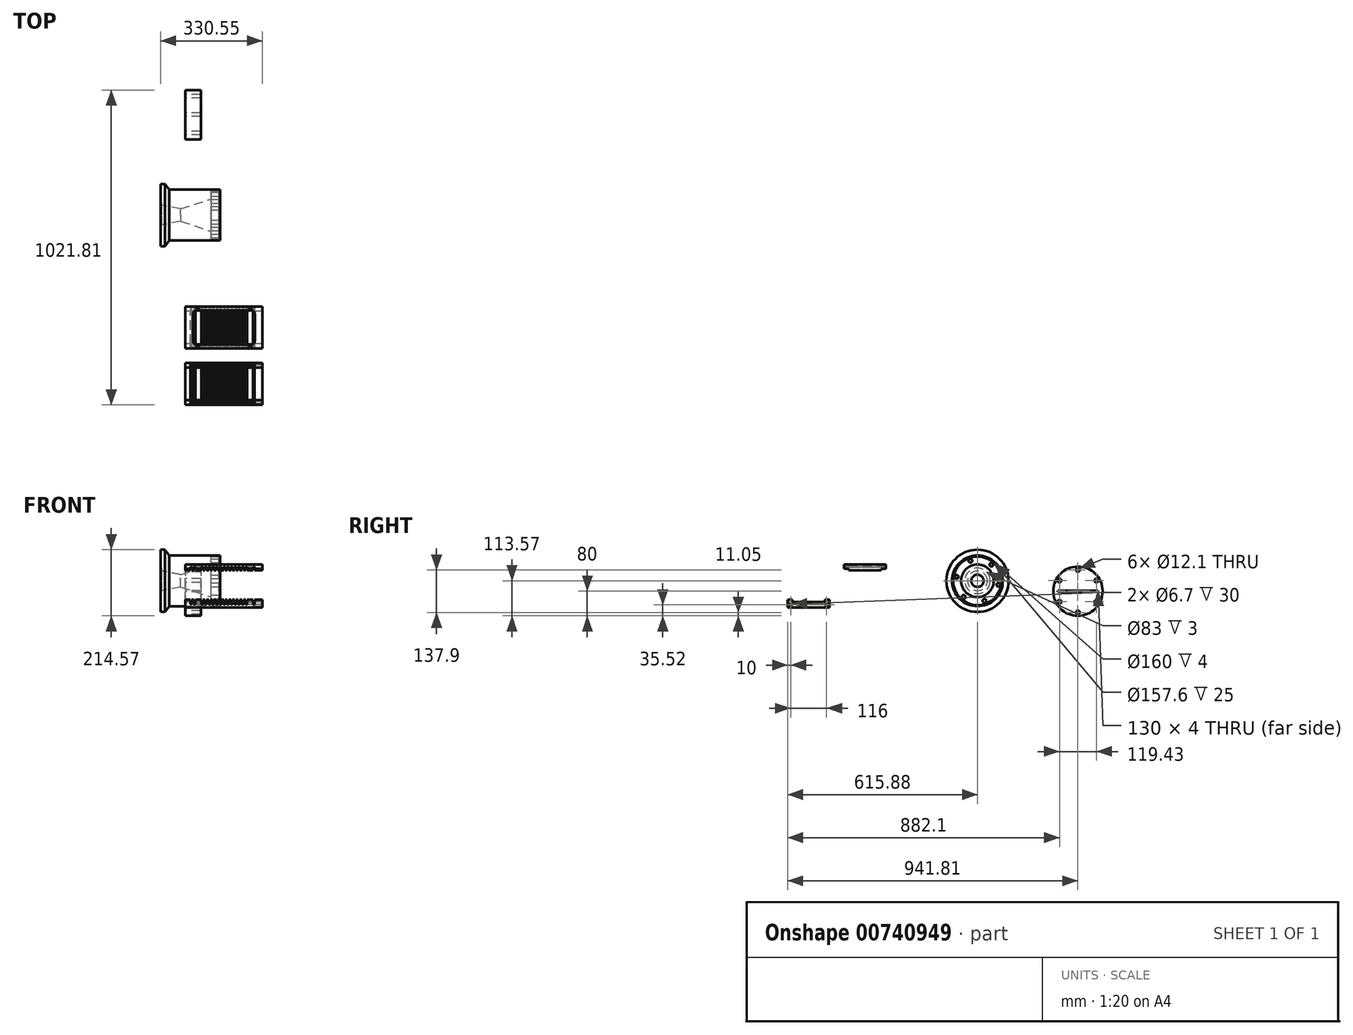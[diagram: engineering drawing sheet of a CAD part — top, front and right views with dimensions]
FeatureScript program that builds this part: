
annotation { "Feature Type Name" : "Feature", "Feature Type Description" : "" }
export const myFeature = defineFeature(function(context is Context, id is Id, definition is map)
    precondition{}
    {
        {
            var Q0;
            Q0=qCreatedBy(makeId("Front.planeOp"),FACE);
            var sketch = newSketch(context, id + "F0", { "sketchPlane" : qUnion([Q0])});
            skLineSegment(sketch, "E0", {"start": v(-80.55, 124) * mm, "end": v(-80.55, 183.5) * mm});
            skLineSegment(sketch, "E1", {"start": v(-80.55, 183.5) * mm, "end": v(-66.55, 183.5) * mm});
            skLineSegment(sketch, "E2", {"start": v(-66.55, 183.5) * mm, "end": v(-52.88, 165) * mm});
            skLineSegment(sketch, "E3", {"start": v(-52.88, 165) * mm, "end": v(-37.88, 165) * mm});
            skLineSegment(sketch, "E4", {"start": v(112.12, 162.5) * mm, "end": v(112.12, 165) * mm});
            skLineSegment(sketch, "E5", {"start": v(112.12, 165) * mm, "end": v(-37.88, 165) * mm});
            skPoint(sketch, "E6.endSnap0", {"position": v(-80.55, 82.5) * mm});
            skLineSegment(sketch, "E7", {"start": v(-261.09, 82.5) * mm, "end": v(-80.55, 82.5) * mm});
            skLineSegment(sketch, "E8", {"start": v(-80.55, 124) * mm, "end": v(-77.55, 124) * mm});
            skLineSegment(sketch, "E9", {"start": v(-77.55, 124) * mm, "end": v(-77.55, 114.5) * mm});
            skLineSegment(sketch, "E10", {"start": v(-77.55, 114.5) * mm, "end": v(-15.38, 102.5) * mm});
            skLineSegment(sketch, "E11", {"start": v(-15.38, 102.5) * mm, "end": v(108.12, 143.67) * mm});
            skPoint(sketch, "E12.orphan", {"position": v(112.12, 82.5) * mm});
            skLineSegment(sketch, "E13.trimOffspring", {"start": v(112.12, 82.5) * mm, "end": v(310.1, 82.5) * mm});
            skLineSegment(sketch, "E14", {"start": v(112.12, 162.5) * mm, "end": v(108.12, 162.5) * mm});
            skLineSegment(sketch, "E15", {"start": v(108.12, 162.5) * mm, "end": v(108.12, 143.67) * mm});
            skPoint(sketch, "E16.orphan", {"position": v(112.12, 145) * mm});
            skSolve(sketch);
        }
        {
            var Q0;
            Q0=makeQuery(id+"F0.imprint","IMPRINT",FACE,{"disambiguationData":[TD([[makeQuery(id+"F0.imprint","IMPRINT",EDGE,{"derivedFrom":sQuery(id+"F0.wireOp",EDGE,"E1")}),-1.0]])]});
            var Q1;
            Q1=sQuery(id+"F0.wireOp",EDGE,"E13.trimOffspring");
            revolve(context, id + "F1", {"entities" : qUnion([Q0]), "axis" : qUnion([Q1]), "revolveType" : RevolveType.ONE_DIRECTION, "angle" : 360 * degree});
        }
        {
            var Q0;
            Q0=makeQuery(id+"F1.opRevolve","SWEPT_FACE",FACE,{"disambiguationData":[OSD([sQuery(id+"F0.wireOp",EDGE,"E15")])]});
            var sketch = newSketch(context, id + "F2", { "sketchPlane" : qUnion([Q0])});
            skSolve(sketch);
        }
        {
            var Q0;
            {var subQ0=sQuery(id+"F0.wireOp",EDGE,"E15");Q0=makeQuery(id+"F2.imprint","IMPRINT",FACE,{"disambiguationData":[TD([[makeQuery(id+"F2.imprint","IMPRINT",EDGE,{"derivedFrom":makeQuery(id+"F1.opRevolve","SWEPT_EDGE",EDGE,{"disambiguationData":[OSD([sQuery(id+"F0.wireOp",EDGE,"E11"),subQ0])]})}),1.0]])]});}
            var sketch = newSketch(context, id + "F3", { "sketchPlane" : qUnion([Q0])});
            skCircle(sketch, "E17", {"center": v(-22.8, 147.57) * mm, "radius": 6 * mm});
            skPoint(sketch, "E18.third.point", {"position": v(-56.7, 43.27) * mm});
            skCircle(sketch, "E19.1.0", {"center": v(-67.75, 95.29) * mm, "radius": 6 * mm});
            skCircle(sketch, "E19.2.0", {"center": v(-44.95, 30.22) * mm, "radius": 6 * mm});
            skCircle(sketch, "E19.3.0", {"center": v(22.8, 17.43) * mm, "radius": 6 * mm});
            skCircle(sketch, "E19.4.0", {"center": v(67.75, 69.71) * mm, "radius": 6 * mm});
            skCircle(sketch, "E19.5.0", {"center": v(44.95, 134.78) * mm, "radius": 6 * mm});
            skPoint(sketch, "E19.center", {"position": v(0, 82.5) * mm});
            skCircle(sketch, "E20", {"center": v(0, 82.5) * mm, "radius": 78.8 * mm});
            skSolve(sketch);
        }
        {
            var Q0;
            Q0=qSketchRegion(id+"F3",true);
            extrude(context, id + "F4", {"entities" : qUnion([Q0]), "operationType" : NewBodyOperationType.REMOVE, "oppositeDirection" : true, "depth" : 25 * mm});
        }
        {
            var Q0;
            Q0=qCreatedBy(makeId("Right.planeOp"),FACE);
            var sketch = newSketch(context, id + "F5", { "sketchPlane" : qUnion([Q0])});
            skCircle(sketch, "E21", {"center": v(325.93, 48.93) * mm, "radius": 80 * mm});
            skLineSegment(sketch, "E22.bottom", {"start": v(260.93, 50.93) * mm, "end": v(390.93, 50.93) * mm});
            skLineSegment(sketch, "E22.top", {"start": v(260.93, 46.93) * mm, "end": v(390.93, 46.93) * mm});
            skLineSegment(sketch, "E22.left", {"start": v(260.93, 50.93) * mm, "end": v(260.93, 46.93) * mm});
            skLineSegment(sketch, "E22.right", {"start": v(390.93, 50.93) * mm, "end": v(390.93, 46.93) * mm});
            skLineSegment(sketch, "E23", {"start": v(325.93, 148.9) * mm, "end": v(325.93, -70.52) * mm, "construction": true});
            skCircle(sketch, "E24", {"center": v(325.93, 117.88) * mm, "radius": 6.05 * mm});
            skCircle(sketch, "E25.1.0", {"center": v(266.22, 83.4) * mm, "radius": 6.05 * mm});
            skCircle(sketch, "E25.2.0", {"center": v(266.22, 14.46) * mm, "radius": 6.05 * mm});
            skCircle(sketch, "E25.3.0", {"center": v(325.93, -20.02) * mm, "radius": 6.05 * mm});
            skCircle(sketch, "E25.4.0", {"center": v(385.65, 14.46) * mm, "radius": 6.05 * mm});
            skCircle(sketch, "E25.5.0", {"center": v(385.65, 83.4) * mm, "radius": 6.05 * mm});
            skSolve(sketch);
        }
        {
            var Q0;
            Q0 = qSketchRegion(id + "F5", true);
            extrude(context, id + "F6", {"entities" : qUnion([Q0]), "depth" : 50 * mm, "offsetDistance" : 25 * mm});
        }
        {
            var Q0;
            Q0=qCreatedBy(makeId("Right.planeOp"),FACE);
            var sketch = newSketch(context, id + "F7", { "sketchPlane" : qUnion([Q0])});
            skLineSegment(sketch, "E26.top", {"start": v(-494.88, 13.45) * mm, "end": v(-600.88, 13.45) * mm});
            skLineSegment(sketch, "E26.left", {"start": v(-494.88, 16.45) * mm, "end": v(-494.88, 13.45) * mm});
            skLineSegment(sketch, "E26.right", {"start": v(-600.88, 16.45) * mm, "end": v(-600.88, 13.45) * mm});
            skPoint(sketch, "E26.middle", {"position": v(-547.88, 14.95) * mm});
            skLineSegment(sketch, "E27", {"start": v(-494.88, 21.45) * mm, "end": v(-484.88, 21.45) * mm});
            skLineSegment(sketch, "E28", {"start": v(-479.88, 16.45) * mm, "end": v(-479.88, -3.55) * mm});
            skLineSegment(sketch, "E29", {"start": v(-547.88, 69.6) * mm, "end": v(-547.88, -62.33) * mm});
            skLineSegment(sketch, "E30", {"start": v(-479.88, -3.55) * mm, "end": v(-547.88, -3.55) * mm});
            skLineSegment(sketch, "E31", {"start": v(-494.88, 16.45) * mm, "end": v(-494.88, 21.45) * mm});
            skLineSegment(sketch, "E32.MirrorCS", {"start": v(-600.88, 16.45) * mm, "end": v(-600.88, 21.45) * mm});
            skLineSegment(sketch, "E33.MirrorCS", {"start": v(-600.88, 21.45) * mm, "end": v(-610.88, 21.45) * mm});
            skLineSegment(sketch, "E34.MirrorCS", {"start": v(-615.88, 16.45) * mm, "end": v(-615.88, -3.55) * mm});
            skLineSegment(sketch, "E35.MirrorCS", {"start": v(-615.88, -3.55) * mm, "end": v(-547.88, -3.55) * mm});
            skLineSegment(sketch, "E36.bottom", {"start": v(-311.68, 116.16) * mm, "end": v(-417.68, 116.16) * mm});
            skLineSegment(sketch, "E36.left", {"start": v(-311.68, 116.16) * mm, "end": v(-311.68, 113.16) * mm});
            skLineSegment(sketch, "E37", {"start": v(-311.68, 121.16) * mm, "end": v(-301.68, 121.16) * mm});
            skLineSegment(sketch, "E38", {"start": v(-311.68, 116.16) * mm, "end": v(-311.68, 121.16) * mm});
            skLineSegment(sketch, "E39.MirrorCS", {"start": v(-417.68, 116.16) * mm, "end": v(-417.68, 121.16) * mm});
            skLineSegment(sketch, "E40.MirrorCS", {"start": v(-417.68, 121.16) * mm, "end": v(-427.68, 121.16) * mm});
            skLineSegment(sketch, "E41", {"start": v(-432.68, 136.16) * mm, "end": v(-296.68, 136.16) * mm});
            skLineSegment(sketch, "E42", {"start": v(-296.68, 136.16) * mm, "end": v(-296.68, 121.16) * mm});
            skLineSegment(sketch, "E43", {"start": v(-364.68, 136.16) * mm, "end": v(-364.68, 116.16) * mm});
            skPoint(sketch, "E43.startSnap0", {"position": v(-364.68, 116.16) * mm});
            skLineSegment(sketch, "E44.MirrorCS", {"start": v(-432.68, 136.16) * mm, "end": v(-432.68, 121.16) * mm});
            skLineSegment(sketch, "E45", {"start": v(-301.68, 121.16) * mm, "end": v(-296.68, 121.16) * mm});
            skPoint(sketch, "E46.orphan", {"position": v(-296.68, 116.16) * mm});
            skPoint(sketch, "E47.end.orphan", {"position": v(-301.68, 116.16) * mm});
            skLineSegment(sketch, "E48", {"start": v(-427.68, 121.16) * mm, "end": v(-432.68, 121.16) * mm});
            skPoint(sketch, "E49.MirrorCS.end.orphan", {"position": v(-427.68, 116.16) * mm});
            skPoint(sketch, "E49.MirrorCS.start.orphan", {"position": v(-427.68, 121.16) * mm});
            skPoint(sketch, "E50.MirrorCS.end.orphan", {"position": v(-432.68, 116.16) * mm});
            skLineSegment(sketch, "E51", {"start": v(-484.88, 21.45) * mm, "end": v(-479.88, 21.45) * mm});
            skLineSegment(sketch, "E52", {"start": v(-479.88, 21.45) * mm, "end": v(-479.88, 16.45) * mm});
            skPoint(sketch, "E53.start.orphan", {"position": v(-484.88, 16.45) * mm});
            skLineSegment(sketch, "E54", {"start": v(-615.88, 16.45) * mm, "end": v(-615.88, 21.45) * mm});
            skLineSegment(sketch, "E55", {"start": v(-615.88, 21.45) * mm, "end": v(-610.88, 21.45) * mm});
            skPoint(sketch, "E56.MirrorCS.end.orphan", {"position": v(-610.88, 16.45) * mm});
            skSolve(sketch);
        }
        {
            var Q0;
            Q0 = qSketchRegion(id + "F7", true);
            extrude(context, id + "F8", {"entities" : qUnion([Q0]), "depth" : 250 * mm, "offsetDistance" : 25 * mm});
        }
        {
            var Q0;
            Q0=makeQuery(id+"F8.opExtrude","SWEPT_FACE",FACE,{"disambiguationData":[OSD([sQuery(id+"F7.wireOp",EDGE,"E41")])]});
            var sketch = newSketch(context, id + "F9", { "sketchPlane" : qUnion([Q0])});
            skPoint(sketch, "E57.startSnap0", {"position": v(0, -364.68) * mm});
            skLineSegment(sketch, "E58.bottom", {"start": v(215, -419.68) * mm, "end": v(35, -419.68) * mm});
            skLineSegment(sketch, "E58.top", {"start": v(215, -309.68) * mm, "end": v(35, -309.68) * mm});
            skLineSegment(sketch, "E58.left", {"start": v(225, -409.68) * mm, "end": v(225, -319.68) * mm});
            skLineSegment(sketch, "E58.right", {"start": v(25, -409.68) * mm, "end": v(25, -319.68) * mm});
            skPoint(sketch, "E58.middle", {"position": v(125, -364.68) * mm});
            skPoint(sketch, "E59.start.orphan", {"position": v(125, -296.68) * mm});
            skPoint(sketch, "E57.start.orphan", {"position": v(-23.66, -364.68) * mm});
            skPoint(sketch, "E60.visualSharp", {"position": v(25, -309.68) * mm});
            skArc(sketch, "E60.filletArc", {"start": v(35, -309.68) * mm, "mid": v(27.93, -312.6) * mm, "end": v(25, -319.68) * mm});
            skPoint(sketch, "E61.visualSharp", {"position": v(25, -419.68) * mm});
            skArc(sketch, "E61.filletArc", {"start": v(25, -409.68) * mm, "mid": v(27.93, -416.75) * mm, "end": v(35, -419.68) * mm});
            skPoint(sketch, "E62.visualSharp", {"position": v(225, -419.68) * mm});
            skArc(sketch, "E62.filletArc", {"start": v(215, -419.68) * mm, "mid": v(222.07, -416.75) * mm, "end": v(225, -409.68) * mm});
            skPoint(sketch, "E63.visualSharp", {"position": v(225, -309.68) * mm});
            skArc(sketch, "E63.filletArc", {"start": v(225, -319.68) * mm, "mid": v(222.07, -312.6) * mm, "end": v(215, -309.68) * mm});
            skSolve(sketch);
        }
        {
            var Q0;
            Q0 = qSketchRegion(id + "F9", true);
            extrude(context, id + "F10", {"entities" : qUnion([Q0]), "operationType" : NewBodyOperationType.REMOVE, "oppositeDirection" : true, "depth" : 10 * mm, "offsetDistance" : 25 * mm});
        }
        {
            var Q0;
            Q0=makeQuery(id+"F8.opExtrude","SWEPT_FACE",FACE,{"disambiguationData":[OSD([sQuery(id+"F7.wireOp",EDGE,"E30"),sQuery(id+"F7.wireOp",EDGE,"E35.MirrorCS")])]});
            var sketch = newSketch(context, id + "F11", { "sketchPlane" : qUnion([Q0])});
            skLineSegment(sketch, "E64.bottom", {"start": v(35, 602.88) * mm, "end": v(215, 602.88) * mm});
            skLineSegment(sketch, "E64.top", {"start": v(35, 492.88) * mm, "end": v(215, 492.88) * mm});
            skLineSegment(sketch, "E64.left", {"start": v(25, 592.88) * mm, "end": v(25, 502.88) * mm});
            skLineSegment(sketch, "E64.right", {"start": v(225, 592.88) * mm, "end": v(225, 502.88) * mm});
            skPoint(sketch, "E64.middle", {"position": v(125, 547.88) * mm});
            skPoint(sketch, "E65.visualSharp", {"position": v(25, 602.88) * mm});
            skArc(sketch, "E65.filletArc", {"start": v(35, 602.88) * mm, "mid": v(27.93, 599.95) * mm, "end": v(25, 592.88) * mm});
            skPoint(sketch, "E66.visualSharp", {"position": v(25, 492.88) * mm});
            skArc(sketch, "E66.filletArc", {"start": v(25, 502.88) * mm, "mid": v(27.93, 495.8) * mm, "end": v(35, 492.88) * mm});
            skPoint(sketch, "E67.visualSharp", {"position": v(225, 492.88) * mm});
            skArc(sketch, "E67.filletArc", {"start": v(215, 492.88) * mm, "mid": v(222.07, 495.8) * mm, "end": v(225, 502.88) * mm});
            skPoint(sketch, "E68.visualSharp", {"position": v(225, 602.88) * mm});
            skArc(sketch, "E68.filletArc", {"start": v(225, 592.88) * mm, "mid": v(222.07, 599.95) * mm, "end": v(215, 602.88) * mm});
            skPoint(sketch, "E69.orphan", {"position": v(125, 615.88) * mm});
            skPoint(sketch, "E70.start.orphan", {"position": v(0, 547.88) * mm});
            skSolve(sketch);
        }
        {
            var Q0;
            Q0 = qSketchRegion(id + "F11", true);
            extrude(context, id + "F12", {"entities" : qUnion([Q0]), "operationType" : NewBodyOperationType.REMOVE, "oppositeDirection" : true, "depth" : 10 * mm, "offsetDistance" : 25 * mm});
        }
        {
            var Q0;
            Q0=makeQuery(id+"F8.opExtrude","CAP_FACE",FACE,{"disambiguationData":[OSD([sQuery(id+"F7.wireOp",EDGE,"E26.bottom"),sQuery(id+"F7.wireOp",EDGE,"E27"),sQuery(id+"F7.wireOp",EDGE,"C7VJGF0Z-FXYF-PAxQ-nA2d-aZA8GV4GVZuc"),sQuery(id+"F7.wireOp",EDGE,"E53"),sQuery(id+"F7.wireOp",EDGE,"E28"),sQuery(id+"F7.wireOp",EDGE,"E30"),sQuery(id+"F7.wireOp",EDGE,"E31"),sQuery(id+"F7.wireOp",EDGE,"E32.MirrorCS"),sQuery(id+"F7.wireOp",EDGE,"E33.MirrorCS"),sQuery(id+"F7.wireOp",EDGE,"E56.MirrorCS"),sQuery(id+"F7.wireOp",EDGE,"2c69a955-ea22-4fbe-a683-bcde0f60a3190.MirrorCS"),sQuery(id+"F7.wireOp",EDGE,"E34.MirrorCS"),sQuery(id+"F7.wireOp",EDGE,"E35.MirrorCS")])],"isStart":false});
            var sketch = newSketch(context, id + "F13", { "sketchPlane" : qUnion([Q0])});
            skCircle(sketch, "E71", {"center": v(-605.88, 4.45) * mm, "radius": 3.35 * mm});
            skCircle(sketch, "E72", {"center": v(-489.88, 4.45) * mm, "radius": 3.35 * mm});
            skSolve(sketch);
        }
        {
            var Q0;
            Q0 = qSketchRegion(id + "F13", true);
            extrude(context, id + "F14", {"entities" : qUnion([Q0]), "operationType" : NewBodyOperationType.REMOVE, "oppositeDirection" : true, "depth" : 30 * mm, "offsetDistance" : 25 * mm});
        }
        {
            var Q0;
            Q0=makeQuery(id+"F8.opExtrude","SWEPT_FACE",FACE,{"disambiguationData":[OSD([sQuery(id+"F7.wireOp",EDGE,"E33.MirrorCS"),sQuery(id+"F7.wireOp",EDGE,"E55")])]});
            var sketch = newSketch(context, id + "F15", { "sketchPlane" : qUnion([Q0])});
            skCircle(sketch, "E73", {"center": v(210, -487.38) * mm, "radius": 3.35 * mm});
            skCircle(sketch, "E74", {"center": v(40, -487.38) * mm, "radius": 3.35 * mm});
            skCircle(sketch, "E75", {"center": v(210, -608.38) * mm, "radius": 3.35 * mm});
            skCircle(sketch, "E76", {"center": v(40, -608.38) * mm, "radius": 3.35 * mm});
            skSolve(sketch);
        }
        {
            var Q0;
            Q0=makeQuery(id+"F15.imprint","IMPRINT",FACE,{"disambiguationData":[TD([[makeQuery(id+"F15.imprint","IMPRINT",EDGE,{"derivedFrom":sQuery(id+"F15.wireOp",EDGE,"E73")}),1.0]])]});
            var Q1;
            Q1=makeQuery(id+"F15.imprint","IMPRINT",FACE,{"disambiguationData":[TD([[makeQuery(id+"F15.imprint","IMPRINT",EDGE,{"derivedFrom":sQuery(id+"F15.wireOp",EDGE,"E74")}),1.0]])]});
            var Q2;
            Q2=makeQuery(id+"F15.imprint","IMPRINT",FACE,{"disambiguationData":[TD([[makeQuery(id+"F15.imprint","IMPRINT",EDGE,{"derivedFrom":sQuery(id+"F15.wireOp",EDGE,"E76")}),1.0]])]});
            var Q3;
            Q3=makeQuery(id+"F15.imprint","IMPRINT",FACE,{"disambiguationData":[TD([[makeQuery(id+"F15.imprint","IMPRINT",EDGE,{"derivedFrom":sQuery(id+"F15.wireOp",EDGE,"E75")}),1.0]])]});
            extrude(context, id + "F16", {"entities" : qUnion([Q0, Q1, Q2, Q3]), "operationType" : NewBodyOperationType.REMOVE, "oppositeDirection" : true, "depth" : 10 * mm, "offsetDistance" : 25 * mm});
        }
        {
            var Q0;
            Q0=makeQuery(id+"F8.opExtrude","SWEPT_FACE",FACE,{"disambiguationData":[OSD([sQuery(id+"F7.wireOp",EDGE,"E41")])]});
            var sketch = newSketch(context, id + "F17", { "sketchPlane" : qUnion([Q0])});
            skLineSegment(sketch, "E77.bottom", {"start": v(40, -304.18) * mm, "end": v(210, -304.18) * mm});
            skLineSegment(sketch, "E77.top", {"start": v(40, -425.18) * mm, "end": v(210, -425.18) * mm});
            skLineSegment(sketch, "E77.left", {"start": v(40, -304.18) * mm, "end": v(40, -425.18) * mm});
            skLineSegment(sketch, "E77.right", {"start": v(210, -304.18) * mm, "end": v(210, -425.18) * mm});
            skPoint(sketch, "E77.middle", {"position": v(125, -364.68) * mm});
            skPoint(sketch, "E77.middle.positionSnap0", {"position": v(125, -296.68) * mm});
            skPoint(sketch, "E77.middle.positionSnap1", {"position": v(0, -364.68) * mm});
            skPoint(sketch, "E77.centerSnap0", {"position": v(125, -296.68) * mm});
            skPoint(sketch, "E77.centerSnap1", {"position": v(0, -364.68) * mm});
            skCircle(sketch, "E78", {"center": v(210, -304.18) * mm, "radius": 4 * mm});
            skCircle(sketch, "E79", {"center": v(40, -304.18) * mm, "radius": 4 * mm});
            skCircle(sketch, "E80", {"center": v(40, -425.18) * mm, "radius": 4 * mm});
            skCircle(sketch, "E81", {"center": v(210, -425.18) * mm, "radius": 4 * mm});
            skSolve(sketch);
        }
        {
            var Q0;
            {var subQ0=sQuery(id+"F17.wireOp",EDGE,"E77.left");var subQ1=sQuery(id+"F17.wireOp",EDGE,"E77.top");var subQ2=makeQuery(id+"F17.imprint","INTERSECT",VERTEX,{"derivedFrom":[subQ1,subQ0]});Q0=makeQuery(id+"F17.imprint","IMPRINT",FACE,{"disambiguationData":[TD([[makeQuery(id+"F17.imprint","IMPRINT",EDGE,{"disambiguationData":[TD([[subQ2,-1.0]])],"derivedFrom":subQ1}),-1.0]])]});}
            var Q1;
            {var subQ0=sQuery(id+"F17.wireOp",EDGE,"E77.left");var subQ1=sQuery(id+"F17.wireOp",EDGE,"E77.top");var subQ2=makeQuery(id+"F17.imprint","INTERSECT",VERTEX,{"derivedFrom":[subQ1,subQ0]});Q1=makeQuery(id+"F17.imprint","IMPRINT",FACE,{"disambiguationData":[TD([[makeQuery(id+"F17.imprint","IMPRINT",EDGE,{"disambiguationData":[TD([[subQ2,-1.0]])],"derivedFrom":subQ1}),1.0]])]});}
            var Q2;
            {var subQ0=sQuery(id+"F17.wireOp",EDGE,"E77.right");var subQ1=sQuery(id+"F17.wireOp",EDGE,"E77.top");var subQ2=makeQuery(id+"F17.imprint","INTERSECT",VERTEX,{"derivedFrom":[subQ1,subQ0]});Q2=makeQuery(id+"F17.imprint","IMPRINT",FACE,{"disambiguationData":[TD([[makeQuery(id+"F17.imprint","IMPRINT",EDGE,{"disambiguationData":[TD([[subQ2,1.0]])],"derivedFrom":subQ1}),-1.0]])]});}
            var Q3;
            {var subQ0=sQuery(id+"F17.wireOp",EDGE,"E77.right");var subQ1=sQuery(id+"F17.wireOp",EDGE,"E77.top");var subQ2=makeQuery(id+"F17.imprint","INTERSECT",VERTEX,{"derivedFrom":[subQ1,subQ0]});Q3=makeQuery(id+"F17.imprint","IMPRINT",FACE,{"disambiguationData":[TD([[makeQuery(id+"F17.imprint","IMPRINT",EDGE,{"disambiguationData":[TD([[subQ2,1.0]])],"derivedFrom":subQ1}),1.0]])]});}
            var Q4;
            {var subQ0=sQuery(id+"F17.wireOp",EDGE,"E77.right");var subQ1=sQuery(id+"F17.wireOp",EDGE,"E77.bottom");var subQ2=makeQuery(id+"F17.imprint","INTERSECT",VERTEX,{"derivedFrom":[subQ1,subQ0]});Q4=makeQuery(id+"F17.imprint","IMPRINT",FACE,{"disambiguationData":[TD([[makeQuery(id+"F17.imprint","IMPRINT",EDGE,{"disambiguationData":[TD([[subQ2,1.0]])],"derivedFrom":subQ1}),1.0]])]});}
            var Q5;
            {var subQ0=sQuery(id+"F17.wireOp",EDGE,"E77.right");var subQ1=sQuery(id+"F17.wireOp",EDGE,"E77.bottom");var subQ2=makeQuery(id+"F17.imprint","INTERSECT",VERTEX,{"derivedFrom":[subQ1,subQ0]});Q5=makeQuery(id+"F17.imprint","IMPRINT",FACE,{"disambiguationData":[TD([[makeQuery(id+"F17.imprint","IMPRINT",EDGE,{"disambiguationData":[TD([[subQ2,1.0]])],"derivedFrom":subQ1}),-1.0]])]});}
            var Q6;
            {var subQ0=sQuery(id+"F17.wireOp",EDGE,"E77.left");var subQ1=sQuery(id+"F17.wireOp",EDGE,"E77.bottom");var subQ2=makeQuery(id+"F17.imprint","INTERSECT",VERTEX,{"derivedFrom":[subQ1,subQ0]});Q6=makeQuery(id+"F17.imprint","IMPRINT",FACE,{"disambiguationData":[TD([[makeQuery(id+"F17.imprint","IMPRINT",EDGE,{"disambiguationData":[TD([[subQ2,-1.0]])],"derivedFrom":subQ1}),1.0]])]});}
            var Q7;
            {var subQ0=sQuery(id+"F17.wireOp",EDGE,"E77.left");var subQ1=sQuery(id+"F17.wireOp",EDGE,"E77.bottom");var subQ2=makeQuery(id+"F17.imprint","INTERSECT",VERTEX,{"derivedFrom":[subQ1,subQ0]});Q7=makeQuery(id+"F17.imprint","IMPRINT",FACE,{"disambiguationData":[TD([[makeQuery(id+"F17.imprint","IMPRINT",EDGE,{"disambiguationData":[TD([[subQ2,-1.0]])],"derivedFrom":subQ1}),-1.0]])]});}
            extrude(context, id + "F18", {"entities" : qUnion([Q0, Q1, Q2, Q3, Q4, Q5, Q6, Q7]), "operationType" : NewBodyOperationType.REMOVE, "oppositeDirection" : true, "depth" : 25 * mm, "offsetDistance" : 25 * mm});
        }
        {
            var Q0;
            Q0=makeQuery(id+"F9.imprint","IMPRINT",FACE,{"disambiguationData":[TD([[makeQuery(id+"F9.imprint","IMPRINT",EDGE,{"derivedFrom":sQuery(id+"F9.wireOp",EDGE,"E58.bottom")}),-1.0]])]});
            extrude(context, id + "F19", {"entities" : qUnion([Q0]), "operationType" : NewBodyOperationType.REMOVE, "oppositeDirection" : true, "depth" : 8 * mm, "offsetDistance" : 25 * mm});
        }
        {
            var Q0;
            Q0=makeQuery(id+"F8.opExtrude","SWEPT_FACE",FACE,{"disambiguationData":[OSD([sQuery(id+"F7.wireOp",EDGE,"E34.MirrorCS"),sQuery(id+"F7.wireOp",EDGE,"E54")])]});
            var sketch = newSketch(context, id + "F20", { "sketchPlane" : qUnion([Q0])});
            skLineSegment(sketch, "E82", {"start": v(250, -3.55) * mm, "end": v(250, 163.65) * mm});
            skLineSegment(sketch, "E83", {"start": v(250, 163.65) * mm, "end": v(235, 163.65) * mm});
            skLineSegment(sketch, "E84", {"start": v(235, 163.65) * mm, "end": v(235, -3.55) * mm});
            skLineSegment(sketch, "E85", {"start": v(235, -3.55) * mm, "end": v(250, -3.55) * mm});
            skLineSegment(sketch, "E86", {"start": v(224.5, -3.55) * mm, "end": v(224.5, 163.65) * mm});
            skLineSegment(sketch, "E87", {"start": v(224.5, 163.65) * mm, "end": v(219.5, 163.65) * mm});
            skLineSegment(sketch, "E88", {"start": v(219.5, 163.65) * mm, "end": v(219.5, -3.55) * mm});
            skLineSegment(sketch, "E89", {"start": v(219.5, -3.55) * mm, "end": v(224.5, -3.55) * mm});
            skLineSegment(sketch, "E90.1.0.0", {"start": v(212.5, -3.55) * mm, "end": v(212.5, 163.65) * mm});
            skLineSegment(sketch, "E90.1.0.1", {"start": v(207.5, 163.65) * mm, "end": v(207.5, -3.55) * mm});
            skLineSegment(sketch, "E90.1.0.2", {"start": v(212.5, 163.65) * mm, "end": v(207.5, 163.65) * mm});
            skLineSegment(sketch, "E90.1.0.3", {"start": v(207.5, -3.55) * mm, "end": v(212.5, -3.55) * mm});
            skLineSegment(sketch, "E90.2.0.0", {"start": v(200.5, -3.55) * mm, "end": v(200.5, 163.65) * mm});
            skLineSegment(sketch, "E90.2.0.1", {"start": v(195.5, 163.65) * mm, "end": v(195.5, -3.55) * mm});
            skLineSegment(sketch, "E90.2.0.2", {"start": v(200.5, 163.65) * mm, "end": v(195.5, 163.65) * mm});
            skLineSegment(sketch, "E90.2.0.3", {"start": v(195.5, -3.55) * mm, "end": v(200.5, -3.55) * mm});
            skLineSegment(sketch, "E90.3.0.0", {"start": v(188.5, -3.55) * mm, "end": v(188.5, 163.65) * mm});
            skLineSegment(sketch, "E90.3.0.1", {"start": v(183.5, 163.65) * mm, "end": v(183.5, -3.55) * mm});
            skLineSegment(sketch, "E90.3.0.2", {"start": v(188.5, 163.65) * mm, "end": v(183.5, 163.65) * mm});
            skLineSegment(sketch, "E90.3.0.3", {"start": v(183.5, -3.55) * mm, "end": v(188.5, -3.55) * mm});
            skLineSegment(sketch, "E90.4.0.0", {"start": v(176.5, -3.55) * mm, "end": v(176.5, 163.65) * mm});
            skLineSegment(sketch, "E90.4.0.1", {"start": v(171.5, 163.65) * mm, "end": v(171.5, -3.55) * mm});
            skLineSegment(sketch, "E90.4.0.2", {"start": v(176.5, 163.65) * mm, "end": v(171.5, 163.65) * mm});
            skLineSegment(sketch, "E90.4.0.3", {"start": v(171.5, -3.55) * mm, "end": v(176.5, -3.55) * mm});
            skLineSegment(sketch, "E90.5.0.0", {"start": v(164.5, -3.55) * mm, "end": v(164.5, 163.65) * mm});
            skLineSegment(sketch, "E90.5.0.1", {"start": v(159.5, 163.65) * mm, "end": v(159.5, -3.55) * mm});
            skLineSegment(sketch, "E90.5.0.2", {"start": v(164.5, 163.65) * mm, "end": v(159.5, 163.65) * mm});
            skLineSegment(sketch, "E90.5.0.3", {"start": v(159.5, -3.55) * mm, "end": v(164.5, -3.55) * mm});
            skLineSegment(sketch, "E90.6.0.0", {"start": v(152.5, -3.55) * mm, "end": v(152.5, 163.65) * mm});
            skLineSegment(sketch, "E90.6.0.1", {"start": v(147.5, 163.65) * mm, "end": v(147.5, -3.55) * mm});
            skLineSegment(sketch, "E90.6.0.2", {"start": v(152.5, 163.65) * mm, "end": v(147.5, 163.65) * mm});
            skLineSegment(sketch, "E90.6.0.3", {"start": v(147.5, -3.55) * mm, "end": v(152.5, -3.55) * mm});
            skLineSegment(sketch, "E90.7.0.0", {"start": v(140.5, -3.55) * mm, "end": v(140.5, 163.65) * mm});
            skLineSegment(sketch, "E90.7.0.1", {"start": v(135.5, 163.65) * mm, "end": v(135.5, -3.55) * mm});
            skLineSegment(sketch, "E90.7.0.2", {"start": v(140.5, 163.65) * mm, "end": v(135.5, 163.65) * mm});
            skLineSegment(sketch, "E90.7.0.3", {"start": v(135.5, -3.55) * mm, "end": v(140.5, -3.55) * mm});
            skLineSegment(sketch, "E90.8.0.0", {"start": v(128.5, -3.55) * mm, "end": v(128.5, 163.65) * mm});
            skLineSegment(sketch, "E90.8.0.1", {"start": v(123.5, 163.65) * mm, "end": v(123.5, -3.55) * mm});
            skLineSegment(sketch, "E90.8.0.2", {"start": v(128.5, 163.65) * mm, "end": v(123.5, 163.65) * mm});
            skLineSegment(sketch, "E90.8.0.3", {"start": v(123.5, -3.55) * mm, "end": v(128.5, -3.55) * mm});
            skLineSegment(sketch, "E90.9.0.0", {"start": v(116.5, -3.55) * mm, "end": v(116.5, 163.65) * mm});
            skLineSegment(sketch, "E90.9.0.1", {"start": v(111.5, 163.65) * mm, "end": v(111.5, -3.55) * mm});
            skLineSegment(sketch, "E90.9.0.2", {"start": v(116.5, 163.65) * mm, "end": v(111.5, 163.65) * mm});
            skLineSegment(sketch, "E90.9.0.3", {"start": v(111.5, -3.55) * mm, "end": v(116.5, -3.55) * mm});
            skLineSegment(sketch, "E90.10.0.0", {"start": v(104.5, -3.55) * mm, "end": v(104.5, 163.65) * mm});
            skLineSegment(sketch, "E90.10.0.1", {"start": v(99.5, 163.65) * mm, "end": v(99.5, -3.55) * mm});
            skLineSegment(sketch, "E90.10.0.2", {"start": v(104.5, 163.65) * mm, "end": v(99.5, 163.65) * mm});
            skLineSegment(sketch, "E90.10.0.3", {"start": v(99.5, -3.55) * mm, "end": v(104.5, -3.55) * mm});
            skLineSegment(sketch, "E90.11.0.0", {"start": v(92.5, -3.55) * mm, "end": v(92.5, 163.65) * mm});
            skLineSegment(sketch, "E90.11.0.1", {"start": v(87.5, 163.65) * mm, "end": v(87.5, -3.55) * mm});
            skLineSegment(sketch, "E90.11.0.2", {"start": v(92.5, 163.65) * mm, "end": v(87.5, 163.65) * mm});
            skLineSegment(sketch, "E90.11.0.3", {"start": v(87.5, -3.55) * mm, "end": v(92.5, -3.55) * mm});
            skLineSegment(sketch, "E90.12.0.0", {"start": v(80.5, -3.55) * mm, "end": v(80.5, 163.65) * mm});
            skLineSegment(sketch, "E90.12.0.1", {"start": v(75.5, 163.65) * mm, "end": v(75.5, -3.55) * mm});
            skLineSegment(sketch, "E90.12.0.2", {"start": v(80.5, 163.65) * mm, "end": v(75.5, 163.65) * mm});
            skLineSegment(sketch, "E90.12.0.3", {"start": v(75.5, -3.55) * mm, "end": v(80.5, -3.55) * mm});
            skLineSegment(sketch, "E90.13.0.0", {"start": v(68.5, -3.55) * mm, "end": v(68.5, 163.65) * mm});
            skLineSegment(sketch, "E90.13.0.1", {"start": v(63.5, 163.65) * mm, "end": v(63.5, -3.55) * mm});
            skLineSegment(sketch, "E90.13.0.2", {"start": v(68.5, 163.65) * mm, "end": v(63.5, 163.65) * mm});
            skLineSegment(sketch, "E90.13.0.3", {"start": v(63.5, -3.55) * mm, "end": v(68.5, -3.55) * mm});
            skLineSegment(sketch, "E90.14.0.0", {"start": v(56.5, -3.55) * mm, "end": v(56.5, 163.65) * mm});
            skLineSegment(sketch, "E90.14.0.1", {"start": v(51.5, 163.65) * mm, "end": v(51.5, -3.55) * mm});
            skLineSegment(sketch, "E90.14.0.2", {"start": v(56.5, 163.65) * mm, "end": v(51.5, 163.65) * mm});
            skLineSegment(sketch, "E90.14.0.3", {"start": v(51.5, -3.55) * mm, "end": v(56.5, -3.55) * mm});
            skLineSegment(sketch, "E90.direction1", {"start": v(224.5, -3.55) * mm, "end": v(212.5, -3.55) * mm, "construction": true});
            skLineSegment(sketch, "E91.0.15.0", {"start": v(44.5, -3.55) * mm, "end": v(44.5, 163.65) * mm});
            skLineSegment(sketch, "E91.3.15.0", {"start": v(39.5, 163.65) * mm, "end": v(39.5, -3.55) * mm});
            skLineSegment(sketch, "E91.6.15.0", {"start": v(44.5, 163.65) * mm, "end": v(39.5, 163.65) * mm});
            skLineSegment(sketch, "E91.9.15.0", {"start": v(39.5, -3.55) * mm, "end": v(44.5, -3.55) * mm});
            skLineSegment(sketch, "E92.0.16.0", {"start": v(32.5, -3.55) * mm, "end": v(32.5, 163.65) * mm});
            skLineSegment(sketch, "E92.3.16.0", {"start": v(27.5, 163.65) * mm, "end": v(27.5, -3.55) * mm});
            skLineSegment(sketch, "E92.6.16.0", {"start": v(32.5, 163.65) * mm, "end": v(27.5, 163.65) * mm});
            skLineSegment(sketch, "E92.9.16.0", {"start": v(27.5, -3.55) * mm, "end": v(32.5, -3.55) * mm});
            skLineSegment(sketch, "E93.0.17.0", {"start": v(20.5, -3.55) * mm, "end": v(20.5, 163.65) * mm});
            skLineSegment(sketch, "E93.3.17.0", {"start": v(15.5, 163.65) * mm, "end": v(15.5, -3.55) * mm});
            skLineSegment(sketch, "E93.6.17.0", {"start": v(20.5, 163.65) * mm, "end": v(15.5, 163.65) * mm});
            skLineSegment(sketch, "E93.9.17.0", {"start": v(15.5, -3.55) * mm, "end": v(20.5, -3.55) * mm});
            skLineSegment(sketch, "E94", {"start": v(15.5, 6.45) * mm, "end": v(224.5, 6.45) * mm});
            skLineSegment(sketch, "E95", {"start": v(15.5, 128.16) * mm, "end": v(224.5, 128.16) * mm});
            skSolve(sketch);
        }
        {
            var Q0;
            {var subQ0=sQuery(id+"F20.wireOp",EDGE,"E95");var subQ5=sQuery(id+"F20.wireOp",EDGE,"E93.3.17.0");var subQ6=makeQuery(id+"F20.imprint","INTERSECT",VERTEX,{"derivedFrom":[subQ5,subQ0]});Q0=makeQuery(id+"F20.imprint","IMPRINT",FACE,{"disambiguationData":[TD([[makeQuery(id+"F20.imprint","IMPRINT",EDGE,{"disambiguationData":[TD([[subQ6,-1.0]])],"derivedFrom":subQ0}),-1.0]])]});}
            var Q1;
            {var subQ0=sQuery(id+"F20.wireOp",EDGE,"E95");var subQ1=sQuery(id+"F20.wireOp",EDGE,"E92.0.16.0");var subQ2=makeQuery(id+"F20.imprint","INTERSECT",VERTEX,{"derivedFrom":[subQ1,subQ0]});Q1=makeQuery(id+"F20.imprint","IMPRINT",FACE,{"disambiguationData":[TD([[makeQuery(id+"F20.imprint","IMPRINT",EDGE,{"disambiguationData":[TD([[subQ2,1.0]])],"derivedFrom":subQ0}),-1.0]])]});}
            var Q2;
            {var subQ0=sQuery(id+"F20.wireOp",EDGE,"E95");var subQ1=sQuery(id+"F20.wireOp",EDGE,"E90.14.0.0");var subQ2=makeQuery(id+"F20.imprint","INTERSECT",VERTEX,{"derivedFrom":[subQ1,subQ0]});Q2=makeQuery(id+"F20.imprint","IMPRINT",FACE,{"disambiguationData":[TD([[makeQuery(id+"F20.imprint","IMPRINT",EDGE,{"disambiguationData":[TD([[subQ2,1.0]])],"derivedFrom":subQ0}),-1.0]])]});}
            var Q3;
            {var subQ0=sQuery(id+"F20.wireOp",EDGE,"E95");var subQ1=sQuery(id+"F20.wireOp",EDGE,"E90.13.0.0");var subQ2=makeQuery(id+"F20.imprint","INTERSECT",VERTEX,{"derivedFrom":[subQ1,subQ0]});Q3=makeQuery(id+"F20.imprint","IMPRINT",FACE,{"disambiguationData":[TD([[makeQuery(id+"F20.imprint","IMPRINT",EDGE,{"disambiguationData":[TD([[subQ2,1.0]])],"derivedFrom":subQ0}),-1.0]])]});}
            var Q4;
            {var subQ0=sQuery(id+"F20.wireOp",EDGE,"E95");var subQ1=sQuery(id+"F20.wireOp",EDGE,"E90.12.0.0");var subQ2=makeQuery(id+"F20.imprint","INTERSECT",VERTEX,{"derivedFrom":[subQ1,subQ0]});Q4=makeQuery(id+"F20.imprint","IMPRINT",FACE,{"disambiguationData":[TD([[makeQuery(id+"F20.imprint","IMPRINT",EDGE,{"disambiguationData":[TD([[subQ2,1.0]])],"derivedFrom":subQ0}),-1.0]])]});}
            var Q5;
            {var subQ0=sQuery(id+"F20.wireOp",EDGE,"E95");var subQ1=sQuery(id+"F20.wireOp",EDGE,"E90.11.0.0");var subQ2=makeQuery(id+"F20.imprint","INTERSECT",VERTEX,{"derivedFrom":[subQ1,subQ0]});Q5=makeQuery(id+"F20.imprint","IMPRINT",FACE,{"disambiguationData":[TD([[makeQuery(id+"F20.imprint","IMPRINT",EDGE,{"disambiguationData":[TD([[subQ2,1.0]])],"derivedFrom":subQ0}),-1.0]])]});}
            var Q6;
            {var subQ0=sQuery(id+"F20.wireOp",EDGE,"E95");var subQ1=sQuery(id+"F20.wireOp",EDGE,"E90.10.0.0");var subQ2=makeQuery(id+"F20.imprint","INTERSECT",VERTEX,{"derivedFrom":[subQ1,subQ0]});Q6=makeQuery(id+"F20.imprint","IMPRINT",FACE,{"disambiguationData":[TD([[makeQuery(id+"F20.imprint","IMPRINT",EDGE,{"disambiguationData":[TD([[subQ2,1.0]])],"derivedFrom":subQ0}),-1.0]])]});}
            var Q7;
            {var subQ0=sQuery(id+"F20.wireOp",EDGE,"E95");var subQ1=sQuery(id+"F20.wireOp",EDGE,"E90.9.0.0");var subQ2=makeQuery(id+"F20.imprint","INTERSECT",VERTEX,{"derivedFrom":[subQ1,subQ0]});Q7=makeQuery(id+"F20.imprint","IMPRINT",FACE,{"disambiguationData":[TD([[makeQuery(id+"F20.imprint","IMPRINT",EDGE,{"disambiguationData":[TD([[subQ2,1.0]])],"derivedFrom":subQ0}),-1.0]])]});}
            var Q8;
            {var subQ0=sQuery(id+"F20.wireOp",EDGE,"E95");var subQ1=sQuery(id+"F20.wireOp",EDGE,"E90.8.0.0");var subQ2=makeQuery(id+"F20.imprint","INTERSECT",VERTEX,{"derivedFrom":[subQ1,subQ0]});Q8=makeQuery(id+"F20.imprint","IMPRINT",FACE,{"disambiguationData":[TD([[makeQuery(id+"F20.imprint","IMPRINT",EDGE,{"disambiguationData":[TD([[subQ2,1.0]])],"derivedFrom":subQ0}),-1.0]])]});}
            var Q9;
            {var subQ0=sQuery(id+"F20.wireOp",EDGE,"E95");var subQ1=sQuery(id+"F20.wireOp",EDGE,"E90.7.0.0");var subQ2=makeQuery(id+"F20.imprint","INTERSECT",VERTEX,{"derivedFrom":[subQ1,subQ0]});Q9=makeQuery(id+"F20.imprint","IMPRINT",FACE,{"disambiguationData":[TD([[makeQuery(id+"F20.imprint","IMPRINT",EDGE,{"disambiguationData":[TD([[subQ2,1.0]])],"derivedFrom":subQ0}),-1.0]])]});}
            var Q10;
            {var subQ0=sQuery(id+"F20.wireOp",EDGE,"E95");var subQ1=sQuery(id+"F20.wireOp",EDGE,"E90.6.0.0");var subQ2=makeQuery(id+"F20.imprint","INTERSECT",VERTEX,{"derivedFrom":[subQ1,subQ0]});Q10=makeQuery(id+"F20.imprint","IMPRINT",FACE,{"disambiguationData":[TD([[makeQuery(id+"F20.imprint","IMPRINT",EDGE,{"disambiguationData":[TD([[subQ2,1.0]])],"derivedFrom":subQ0}),-1.0]])]});}
            var Q11;
            {var subQ0=sQuery(id+"F20.wireOp",EDGE,"E95");var subQ1=sQuery(id+"F20.wireOp",EDGE,"E90.5.0.0");var subQ2=makeQuery(id+"F20.imprint","INTERSECT",VERTEX,{"derivedFrom":[subQ1,subQ0]});Q11=makeQuery(id+"F20.imprint","IMPRINT",FACE,{"disambiguationData":[TD([[makeQuery(id+"F20.imprint","IMPRINT",EDGE,{"disambiguationData":[TD([[subQ2,1.0]])],"derivedFrom":subQ0}),-1.0]])]});}
            var Q12;
            {var subQ0=sQuery(id+"F20.wireOp",EDGE,"E95");var subQ1=sQuery(id+"F20.wireOp",EDGE,"E90.4.0.0");var subQ2=makeQuery(id+"F20.imprint","INTERSECT",VERTEX,{"derivedFrom":[subQ1,subQ0]});Q12=makeQuery(id+"F20.imprint","IMPRINT",FACE,{"disambiguationData":[TD([[makeQuery(id+"F20.imprint","IMPRINT",EDGE,{"disambiguationData":[TD([[subQ2,1.0]])],"derivedFrom":subQ0}),-1.0]])]});}
            var Q13;
            {var subQ0=sQuery(id+"F20.wireOp",EDGE,"E95");var subQ1=sQuery(id+"F20.wireOp",EDGE,"E90.3.0.0");var subQ2=makeQuery(id+"F20.imprint","INTERSECT",VERTEX,{"derivedFrom":[subQ1,subQ0]});Q13=makeQuery(id+"F20.imprint","IMPRINT",FACE,{"disambiguationData":[TD([[makeQuery(id+"F20.imprint","IMPRINT",EDGE,{"disambiguationData":[TD([[subQ2,1.0]])],"derivedFrom":subQ0}),-1.0]])]});}
            var Q14;
            {var subQ0=sQuery(id+"F20.wireOp",EDGE,"E95");var subQ1=sQuery(id+"F20.wireOp",EDGE,"E90.2.0.0");var subQ2=makeQuery(id+"F20.imprint","INTERSECT",VERTEX,{"derivedFrom":[subQ1,subQ0]});Q14=makeQuery(id+"F20.imprint","IMPRINT",FACE,{"disambiguationData":[TD([[makeQuery(id+"F20.imprint","IMPRINT",EDGE,{"disambiguationData":[TD([[subQ2,1.0]])],"derivedFrom":subQ0}),-1.0]])]});}
            var Q15;
            {var subQ0=sQuery(id+"F20.wireOp",EDGE,"E95");var subQ1=sQuery(id+"F20.wireOp",EDGE,"E86");var subQ2=makeQuery(id+"F20.imprint","INTERSECT",VERTEX,{"derivedFrom":[subQ1,subQ0]});Q15=makeQuery(id+"F20.imprint","IMPRINT",FACE,{"disambiguationData":[TD([[makeQuery(id+"F20.imprint","IMPRINT",EDGE,{"disambiguationData":[TD([[subQ2,1.0]])],"derivedFrom":subQ0}),-1.0]])]});}
            var Q16;
            {var subQ0=sQuery(id+"F20.wireOp",EDGE,"E94");var subQ1=sQuery(id+"F20.wireOp",EDGE,"E86");var subQ2=makeQuery(id+"F20.imprint","INTERSECT",VERTEX,{"derivedFrom":[subQ1,subQ0]});Q16=makeQuery(id+"F20.imprint","IMPRINT",FACE,{"disambiguationData":[TD([[makeQuery(id+"F20.imprint","IMPRINT",EDGE,{"disambiguationData":[TD([[subQ2,1.0]])],"derivedFrom":subQ0}),1.0]])]});}
            var Q17;
            {var subQ0=sQuery(id+"F20.wireOp",EDGE,"E94");var subQ1=sQuery(id+"F20.wireOp",EDGE,"E90.2.0.0");var subQ2=makeQuery(id+"F20.imprint","INTERSECT",VERTEX,{"derivedFrom":[subQ1,subQ0]});Q17=makeQuery(id+"F20.imprint","IMPRINT",FACE,{"disambiguationData":[TD([[makeQuery(id+"F20.imprint","IMPRINT",EDGE,{"disambiguationData":[TD([[subQ2,1.0]])],"derivedFrom":subQ0}),1.0]])]});}
            var Q18;
            {var subQ0=sQuery(id+"F20.wireOp",EDGE,"E94");var subQ1=sQuery(id+"F20.wireOp",EDGE,"E90.3.0.0");var subQ2=makeQuery(id+"F20.imprint","INTERSECT",VERTEX,{"derivedFrom":[subQ1,subQ0]});Q18=makeQuery(id+"F20.imprint","IMPRINT",FACE,{"disambiguationData":[TD([[makeQuery(id+"F20.imprint","IMPRINT",EDGE,{"disambiguationData":[TD([[subQ2,1.0]])],"derivedFrom":subQ0}),1.0]])]});}
            var Q19;
            {var subQ0=sQuery(id+"F20.wireOp",EDGE,"E94");var subQ1=sQuery(id+"F20.wireOp",EDGE,"E90.4.0.0");var subQ2=makeQuery(id+"F20.imprint","INTERSECT",VERTEX,{"derivedFrom":[subQ1,subQ0]});Q19=makeQuery(id+"F20.imprint","IMPRINT",FACE,{"disambiguationData":[TD([[makeQuery(id+"F20.imprint","IMPRINT",EDGE,{"disambiguationData":[TD([[subQ2,1.0]])],"derivedFrom":subQ0}),1.0]])]});}
            var Q20;
            {var subQ0=sQuery(id+"F20.wireOp",EDGE,"E94");var subQ1=sQuery(id+"F20.wireOp",EDGE,"E90.5.0.0");var subQ2=makeQuery(id+"F20.imprint","INTERSECT",VERTEX,{"derivedFrom":[subQ1,subQ0]});Q20=makeQuery(id+"F20.imprint","IMPRINT",FACE,{"disambiguationData":[TD([[makeQuery(id+"F20.imprint","IMPRINT",EDGE,{"disambiguationData":[TD([[subQ2,1.0]])],"derivedFrom":subQ0}),1.0]])]});}
            var Q21;
            {var subQ0=sQuery(id+"F20.wireOp",EDGE,"E94");var subQ1=sQuery(id+"F20.wireOp",EDGE,"E90.6.0.0");var subQ2=makeQuery(id+"F20.imprint","INTERSECT",VERTEX,{"derivedFrom":[subQ1,subQ0]});Q21=makeQuery(id+"F20.imprint","IMPRINT",FACE,{"disambiguationData":[TD([[makeQuery(id+"F20.imprint","IMPRINT",EDGE,{"disambiguationData":[TD([[subQ2,1.0]])],"derivedFrom":subQ0}),1.0]])]});}
            var Q22;
            {var subQ0=sQuery(id+"F20.wireOp",EDGE,"E94");var subQ1=sQuery(id+"F20.wireOp",EDGE,"E90.7.0.0");var subQ2=makeQuery(id+"F20.imprint","INTERSECT",VERTEX,{"derivedFrom":[subQ1,subQ0]});Q22=makeQuery(id+"F20.imprint","IMPRINT",FACE,{"disambiguationData":[TD([[makeQuery(id+"F20.imprint","IMPRINT",EDGE,{"disambiguationData":[TD([[subQ2,1.0]])],"derivedFrom":subQ0}),1.0]])]});}
            var Q23;
            {var subQ0=sQuery(id+"F20.wireOp",EDGE,"E94");var subQ1=sQuery(id+"F20.wireOp",EDGE,"E90.8.0.0");var subQ2=makeQuery(id+"F20.imprint","INTERSECT",VERTEX,{"derivedFrom":[subQ1,subQ0]});Q23=makeQuery(id+"F20.imprint","IMPRINT",FACE,{"disambiguationData":[TD([[makeQuery(id+"F20.imprint","IMPRINT",EDGE,{"disambiguationData":[TD([[subQ2,1.0]])],"derivedFrom":subQ0}),1.0]])]});}
            var Q24;
            {var subQ0=sQuery(id+"F20.wireOp",EDGE,"E94");var subQ1=sQuery(id+"F20.wireOp",EDGE,"E90.9.0.0");var subQ2=makeQuery(id+"F20.imprint","INTERSECT",VERTEX,{"derivedFrom":[subQ1,subQ0]});Q24=makeQuery(id+"F20.imprint","IMPRINT",FACE,{"disambiguationData":[TD([[makeQuery(id+"F20.imprint","IMPRINT",EDGE,{"disambiguationData":[TD([[subQ2,1.0]])],"derivedFrom":subQ0}),1.0]])]});}
            var Q25;
            {var subQ0=sQuery(id+"F20.wireOp",EDGE,"E94");var subQ1=sQuery(id+"F20.wireOp",EDGE,"E90.10.0.0");var subQ2=makeQuery(id+"F20.imprint","INTERSECT",VERTEX,{"derivedFrom":[subQ1,subQ0]});Q25=makeQuery(id+"F20.imprint","IMPRINT",FACE,{"disambiguationData":[TD([[makeQuery(id+"F20.imprint","IMPRINT",EDGE,{"disambiguationData":[TD([[subQ2,1.0]])],"derivedFrom":subQ0}),1.0]])]});}
            var Q26;
            {var subQ0=sQuery(id+"F20.wireOp",EDGE,"E94");var subQ1=sQuery(id+"F20.wireOp",EDGE,"E90.11.0.0");var subQ2=makeQuery(id+"F20.imprint","INTERSECT",VERTEX,{"derivedFrom":[subQ1,subQ0]});Q26=makeQuery(id+"F20.imprint","IMPRINT",FACE,{"disambiguationData":[TD([[makeQuery(id+"F20.imprint","IMPRINT",EDGE,{"disambiguationData":[TD([[subQ2,1.0]])],"derivedFrom":subQ0}),1.0]])]});}
            var Q27;
            {var subQ0=sQuery(id+"F20.wireOp",EDGE,"E94");var subQ1=sQuery(id+"F20.wireOp",EDGE,"E90.12.0.0");var subQ2=makeQuery(id+"F20.imprint","INTERSECT",VERTEX,{"derivedFrom":[subQ1,subQ0]});Q27=makeQuery(id+"F20.imprint","IMPRINT",FACE,{"disambiguationData":[TD([[makeQuery(id+"F20.imprint","IMPRINT",EDGE,{"disambiguationData":[TD([[subQ2,1.0]])],"derivedFrom":subQ0}),1.0]])]});}
            var Q28;
            {var subQ0=sQuery(id+"F20.wireOp",EDGE,"E94");var subQ1=sQuery(id+"F20.wireOp",EDGE,"E90.13.0.0");var subQ2=makeQuery(id+"F20.imprint","INTERSECT",VERTEX,{"derivedFrom":[subQ1,subQ0]});Q28=makeQuery(id+"F20.imprint","IMPRINT",FACE,{"disambiguationData":[TD([[makeQuery(id+"F20.imprint","IMPRINT",EDGE,{"disambiguationData":[TD([[subQ2,1.0]])],"derivedFrom":subQ0}),1.0]])]});}
            var Q29;
            {var subQ0=sQuery(id+"F20.wireOp",EDGE,"E94");var subQ1=sQuery(id+"F20.wireOp",EDGE,"E90.14.0.0");var subQ2=makeQuery(id+"F20.imprint","INTERSECT",VERTEX,{"derivedFrom":[subQ1,subQ0]});Q29=makeQuery(id+"F20.imprint","IMPRINT",FACE,{"disambiguationData":[TD([[makeQuery(id+"F20.imprint","IMPRINT",EDGE,{"disambiguationData":[TD([[subQ2,1.0]])],"derivedFrom":subQ0}),1.0]])]});}
            var Q30;
            {var subQ0=sQuery(id+"F20.wireOp",EDGE,"E94");var subQ1=sQuery(id+"F20.wireOp",EDGE,"E92.0.16.0");var subQ2=makeQuery(id+"F20.imprint","INTERSECT",VERTEX,{"derivedFrom":[subQ1,subQ0]});Q30=makeQuery(id+"F20.imprint","IMPRINT",FACE,{"disambiguationData":[TD([[makeQuery(id+"F20.imprint","IMPRINT",EDGE,{"disambiguationData":[TD([[subQ2,1.0]])],"derivedFrom":subQ0}),1.0]])]});}
            var Q31;
            {var subQ0=sQuery(id+"F20.wireOp",EDGE,"E94");var subQ5=sQuery(id+"F20.wireOp",EDGE,"E93.3.17.0");var subQ6=makeQuery(id+"F20.imprint","INTERSECT",VERTEX,{"derivedFrom":[subQ5,subQ0]});Q31=makeQuery(id+"F20.imprint","IMPRINT",FACE,{"disambiguationData":[TD([[makeQuery(id+"F20.imprint","IMPRINT",EDGE,{"disambiguationData":[TD([[subQ6,-1.0]])],"derivedFrom":subQ0}),1.0]])]});}
            extrude(context, id + "F21", {"entities" : qUnion([Q0, Q1, Q2, Q3, Q4, Q5, Q6, Q7, Q8, Q9, Q10, Q11, Q12, Q13, Q14, Q15, Q16, Q17, Q18, Q19, Q20, Q21, Q22, Q23, Q24, Q25, Q26, Q27, Q28, Q29, Q30, Q31]), "operationType" : NewBodyOperationType.REMOVE, "oppositeDirection" : true, "depth" : 338 * mm, "offsetDistance" : 25 * mm});
        }
    });
